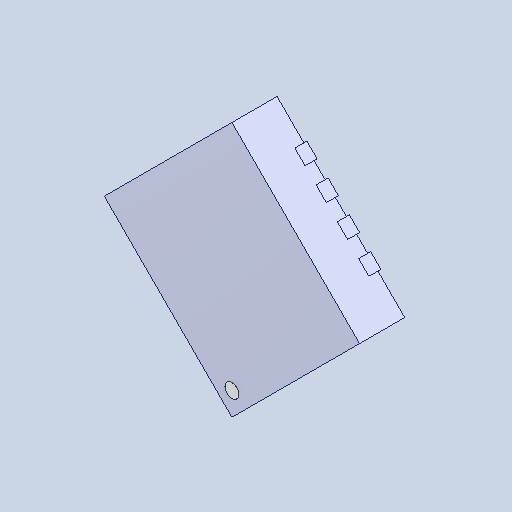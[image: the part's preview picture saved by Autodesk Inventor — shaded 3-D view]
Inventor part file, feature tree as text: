
AUTODESK INVENTOR PART (.ipt)
format: ipt  version: 2025 (Build 290162000, 162)  size: 232,448 bytes
history: native  units: mm
features: other x17, chamfer x2
ambient origin geometry x8: Origin, YZ Plane, XZ Plane, XY Plane, X Axis, Y Axis, Z Axis, Center Point
bodies: Solid1 (feature_tree), Solid2 (feature_tree), Solid3 (feature_tree), Solid4 (feature_tree), Solid5 (feature_tree), Solid6 (feature_tree), Solid7 (feature_tree), Solid8 (feature_tree), Solid9 (feature_tree), Solid10 (feature_tree), Solid11 (feature_tree), Solid12 (feature_tree), Solid13 (feature_tree), Solid14 (feature_tree), Solid15 (feature_tree), Solid16 (feature_tree), Solid17 (feature_tree), Solid18 (feature_tree), Solid19 (feature_tree)
feature tree (19):
  other  "LPattern4[4]"
  other  "LPattern3[4]"
  chamfer  "Chamfer2"  [1 undecoded]
  other  "LPattern4[1]"
  chamfer  "Chamfer1"  [1 undecoded]
  other  "Boss-Extrude2[2]"
  other  "LPattern3[3]"
  other  "LPattern4[5]"
  other  "Boss-Extrude3[2]"
  other  "LPattern3[5]"
  other  "LPattern4[3]"
  other  "LPattern3[1]"
  other  "Boss-Extrude3[1]"
  other  "LPattern4[2]"
  other  "LPattern3[6]"
  other  "LPattern3[2]"
  other  "LPattern4[6]"
  other  "Boss-Extrude2[1]"
  other  "PIN1"
note: 2 required parameter values undecoded (feature->parameter linkage not recoverable at this tier; creation-order binding heuristic only, values carry confidence <= 0.55)
